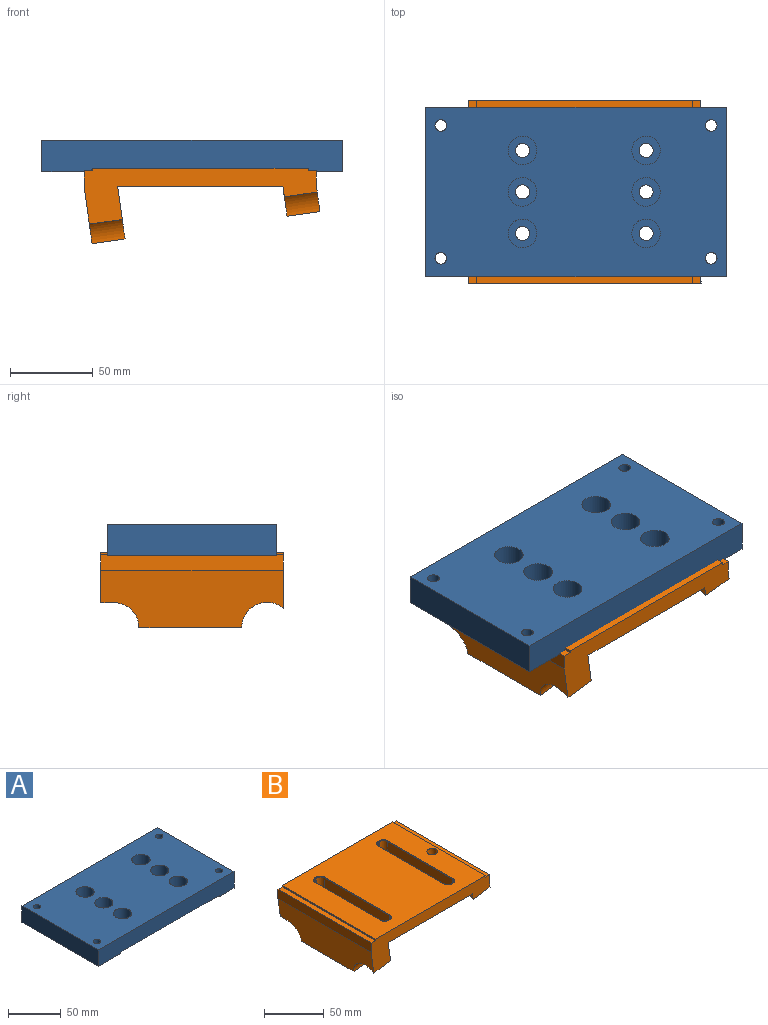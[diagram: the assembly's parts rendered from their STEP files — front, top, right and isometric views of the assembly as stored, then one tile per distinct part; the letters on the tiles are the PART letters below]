
ASSEMBLY  parts=2 mates=1
PART A: 40 faces, bbox 181x102x19 mm
  f0: plane 102x20mm, normal (0,0,-1), area 1721mm2, adj f1,f8,f9,f33,f36,f37
  f1: plane 181x19mm, normal (0,-1,0), area 3242.5mm2, adj f0,f8,f10,f11,f12,f37,f38,f39
  f2: cylinder r=4.25mm len=8.5mm, axis (0,0,1), area 146.9mm2, adj f13,f39
  f3: cylinder r=4.25mm len=8.5mm, axis (0,0,1), area 146.9mm2, adj f15,f39
  f4: cylinder r=4.25mm len=8.5mm, axis (0,0,1), area 146.9mm2, adj f17,f39
  f5: cylinder r=4.25mm len=8.5mm, axis (0,0,1), area 146.9mm2, adj f19,f39
  f6: cylinder r=4.25mm len=8.5mm, axis (0,0,1), area 146.9mm2, adj f21,f39
  f7: cylinder r=4.25mm len=8.5mm, axis (0,0,1), area 146.9mm2, adj f23,f39
  f8: plane 102x19mm, normal (1,0,0), area 1938mm2, adj f0,f1,f9,f11
  f9: plane 181x19mm, normal (0,1,0), area 3242.5mm2, adj f0,f8,f10,f11,f12,f37,f38,f39
  f10: plane 102x19mm, normal (-1,0,0), area 1938mm2, adj f1,f9,f11,f12
  f11: plane 181x102mm, normal (0,0,1), area 16905.8mm2, adj f1,f8,f9,f10,f14,f16,f18,f20
  f12: plane 102x30mm, normal (0,0,-1), area 2741mm2, adj f1,f9,f10,f27,f30,f38
  f13: plane 17.25x17.25mm, normal (0,0,1), area 177mm2, adj f2,f14
  f14: cylinder r=8.62mm len=17.25mm, axis (0,0,1), area 650.3mm2, adj f11,f13
  f15: plane 17.25x17.25mm, normal (0,0,1), area 177mm2, adj f3,f16
  f16: cylinder r=8.62mm len=17.25mm, axis (0,0,1), area 650.3mm2, adj f11,f15
  f17: plane 17.25x17.25mm, normal (0,0,1), area 177mm2, adj f4,f18
  f18: cylinder r=8.62mm len=17.25mm, axis (0,0,1), area 650.3mm2, adj f11,f17
  f19: plane 17.25x17.25mm, normal (0,0,1), area 177mm2, adj f5,f20
  f20: cylinder r=8.62mm len=17.25mm, axis (0,0,1), area 650.3mm2, adj f11,f19
  f21: plane 17.25x17.25mm, normal (0,0,1), area 177mm2, adj f6,f22
  f22: cylinder r=8.62mm len=17.25mm, axis (0,0,1), area 650.3mm2, adj f11,f21
  f23: plane 17.25x17.25mm, normal (0,0,1), area 177mm2, adj f7,f24
  f24: cylinder r=8.62mm len=17.25mm, axis (0,0,1), area 650.3mm2, adj f11,f23
  f25: cylinder r=3.5mm len=11mm, axis (0,0,-1), area 241.9mm2, adj f11,f26
  f26: plane 14.25x14.25mm, normal (0,0,-1), area 121mm2, adj f25,f27
  f27: cylinder r=7.12mm len=14.25mm, axis (0,0,-1), area 358.1mm2, adj f12,f26
  f28: cylinder r=3.5mm len=11mm, axis (0,0,-1), area 241.9mm2, adj f11,f29
  f29: plane 14.25x14.25mm, normal (0,0,-1), area 121mm2, adj f28,f30
  f30: cylinder r=7.12mm len=14.25mm, axis (0,0,-1), area 358.1mm2, adj f12,f29
  f31: cylinder r=3.5mm len=11mm, axis (0,0,-1), area 241.9mm2, adj f11,f32
  f32: plane 14.25x14.25mm, normal (0,0,-1), area 121mm2, adj f31,f33
  f33: cylinder r=7.12mm len=14.25mm, axis (0,0,-1), area 358.1mm2, adj f0,f32
  f34: cylinder r=3.5mm len=11mm, axis (0,0,-1), area 241.9mm2, adj f11,f35
  f35: plane 14.25x14.25mm, normal (0,0,-1), area 121mm2, adj f34,f36
  f36: cylinder r=7.12mm len=14.25mm, axis (0,0,-1), area 358.1mm2, adj f0,f35
  f37: plane 102x1.5mm, normal (-1,0,0), area 153mm2, adj f0,f1,f9,f39
  f38: plane 102x1.5mm, normal (1,0,0), area 153mm2, adj f1,f9,f12,f39
  f39: plane 131x102mm, normal (0,0,-1), area 13021.5mm2, adj f1,f2,f3,f4,f5,f6,f7,f9
PART B: 74 faces, bbox 142.4x110.3x47 mm
  f0: plane 130.27x110.27mm, normal (0,0,1), area 12364.7mm2, adj f1,f12,f53,f54,f55,f56,f57,f58
  f1: plane 140.48x33.73mm, normal (0,-1,0), area 2053.4mm2, adj f0,f2,f4,f5,f6,f7,f9,f10
  f2: plane 110x99.61mm, normal (0,0,-1), area 9085.7mm2, adj f1,f9,f10,f12,f37,f38,f39,f40
  f3: plane 98.95x15.18mm, normal (0.99,0,0.14), area 1051.1mm2, adj f6,f11,f12,f14,f15,f16
  f4: plane 110x34.47mm, normal (-0.99,0,-0.14), area 3204.6mm2, adj f1,f7,f8,f12,f13,f17,f18
  f5: plane 8.46x3.44mm, normal (0.99,0,0.14), area 10.4mm2, adj f1,f6,f14
  f6: plane 110.02x9.52mm, normal (1,0,0), area 1044.9mm2, adj f1,f3,f5,f12,f14,f71
  f7: plane 110x9.5mm, normal (-1,0,0), area 1045mm2, adj f1,f4,f12,f73
  f8: plane 62x19.81mm, normal (0.14,0,-0.99), area 1176.4mm2, adj f4,f9,f13,f17,f28
  f9: plane 110x31.69mm, normal (0.99,0,0.14), area 2895.4mm2, adj f1,f2,f8,f12,f13,f17,f18
  f10: plane 110x17.96mm, normal (-0.99,0,-0.14), area 1370.5mm2, adj f1,f2,f11,f12,f14,f15,f16
  f11: plane 62x19.81mm, normal (0.14,0,-0.99), area 1176.4mm2, adj f3,f10,f14,f15,f69
  f12: plane 140.01x30.38mm, normal (0,1,0), area 1918.2mm2, adj f0,f2,f3,f4,f6,f7,f9,f10
  f13: cylinder r=15.25mm len=25mm, axis (-0.99,0,-0.14), area 693.3mm2, adj f1,f4,f8,f9
  f14: cylinder r=15.25mm len=25mm, axis (-0.99,0,-0.14), area 693.3mm2, adj f1,f3,f5,f6,f10,f11
  f15: cylinder r=15.25mm len=21.93mm, axis (-0.99,0,-0.14), area 479.1mm2, adj f3,f10,f11,f16
  f16: plane 19.81x7.75mm, normal (0.14,0,-0.99), area 155mm2, adj f3,f10,f12,f15
  f17: cylinder r=15.25mm len=21.93mm, axis (-0.99,0,-0.14), area 479.1mm2, adj f4,f8,f9,f18
  f18: plane 19.81x7.75mm, normal (0.14,0,-0.99), area 155mm2, adj f4,f9,f12,f17
  f19: plane 10x1mm, normal (0,1,0), area 10mm2, adj f29,f32,f48,f56
  f20: plane 77x10mm, normal (-1,0,0), area 770mm2, adj f29,f30,f45,f53
  f21: plane 10x1mm, normal (0,-1,0), area 10mm2, adj f30,f31,f49,f57
  f22: plane 77x10mm, normal (1,0,0), area 770mm2, adj f31,f32,f52,f60
  f23: plane 10x1mm, normal (0,1,0), area 10mm2, adj f33,f36,f39,f67
  f24: plane 77x10mm, normal (-1,0,0), area 770mm2, adj f35,f36,f38,f66
  f25: plane 10x1mm, normal (0,-1,0), area 10mm2, adj f34,f35,f42,f62
  f26: plane 77x10mm, normal (1,0,0), area 770mm2, adj f33,f34,f43,f63
  f27: cone r=0mm half-angle=59deg, axis (0.14,0,-0.99), area 74.2mm2, adj f28
  f28: cylinder r=4.5mm len=33.93mm, axis (0.14,0,-0.99), area 933.1mm2, adj f8,f27
  f29: cylinder r=4.5mm len=10mm, axis (0,0,1), area 70.7mm2, adj f19,f20,f46,f54
  f30: cylinder r=4.5mm len=10mm, axis (0,0,-1), area 70.7mm2, adj f20,f21,f47,f55
  f31: cylinder r=4.5mm len=10mm, axis (0,0,1), area 70.7mm2, adj f21,f22,f51,f59
  f32: cylinder r=4.5mm len=10mm, axis (0,0,-1), area 70.7mm2, adj f19,f22,f50,f58
  f33: cylinder r=4.5mm len=10mm, axis (0,0,-1), area 70.7mm2, adj f23,f26,f41,f65
  f34: cylinder r=4.5mm len=10mm, axis (0,0,1), area 70.7mm2, adj f25,f26,f44,f61
  f35: cylinder r=4.5mm len=10mm, axis (0,0,-1), area 70.7mm2, adj f24,f25,f40,f64
  f36: cylinder r=4.5mm len=10mm, axis (0,0,1), area 70.7mm2, adj f23,f24,f37,f68
  f37: torus R=5mm, axis (0,0,1), area 5.8mm2, adj f2,f36,f38,f39
  f38: cylinder r=0.5mm len=77mm, axis (0,1,0), area 60.5mm2, adj f2,f24,f37,f40
  f39: cylinder r=0.5mm len=1mm, axis (1,0,0), area 0.8mm2, adj f2,f23,f37,f41
  f40: torus R=5mm, axis (0,0,1), area 5.8mm2, adj f2,f35,f38,f42
  f41: torus R=5mm, axis (0,0,1), area 5.8mm2, adj f2,f33,f39,f43
  f42: cylinder r=0.5mm len=1mm, axis (-1,0,0), area 0.8mm2, adj f2,f25,f40,f44
  f43: cylinder r=0.5mm len=77mm, axis (0,-1,0), area 60.5mm2, adj f2,f26,f41,f44
  f44: torus R=5mm, axis (0,0,1), area 5.8mm2, adj f2,f34,f42,f43
  f45: cylinder r=0.5mm len=77mm, axis (0,1,0), area 60.5mm2, adj f2,f20,f46,f47
  f46: torus R=5mm, axis (0,0,1), area 5.8mm2, adj f2,f29,f45,f48
  f47: torus R=5mm, axis (0,0,1), area 5.8mm2, adj f2,f30,f45,f49
  f48: cylinder r=0.5mm len=1mm, axis (1,0,0), area 0.8mm2, adj f2,f19,f46,f50
  f49: cylinder r=0.5mm len=1mm, axis (-1,0,0), area 0.8mm2, adj f2,f21,f47,f51
  f50: torus R=5mm, axis (0,0,1), area 5.8mm2, adj f2,f32,f48,f52
  f51: torus R=5mm, axis (0,0,1), area 5.8mm2, adj f2,f31,f49,f52
  f52: cylinder r=0.5mm len=77mm, axis (0,-1,0), area 60.5mm2, adj f2,f22,f50,f51
  f53: cylinder r=0.5mm len=77mm, axis (0,-1,0), area 60.5mm2, adj f0,f20,f54,f55
  f54: torus R=5mm, axis (0,0,1), area 5.8mm2, adj f0,f29,f53,f56
  f55: torus R=5mm, axis (0,0,1), area 5.8mm2, adj f0,f30,f53,f57
  f56: cylinder r=0.5mm len=1mm, axis (-1,0,0), area 0.8mm2, adj f0,f19,f54,f58
  f57: cylinder r=0.5mm len=1mm, axis (1,0,0), area 0.8mm2, adj f0,f21,f55,f59
  f58: torus R=5mm, axis (0,0,1), area 5.8mm2, adj f0,f32,f56,f60
  f59: torus R=5mm, axis (0,0,1), area 5.8mm2, adj f0,f31,f57,f60
  f60: cylinder r=0.5mm len=77mm, axis (0,1,0), area 60.5mm2, adj f0,f22,f58,f59
  f61: torus R=5mm, axis (0,0,1), area 5.8mm2, adj f0,f34,f62,f63
  f62: cylinder r=0.5mm len=1mm, axis (1,0,0), area 0.8mm2, adj f0,f25,f61,f64
  f63: cylinder r=0.5mm len=77mm, axis (0,1,0), area 60.5mm2, adj f0,f26,f61,f65
  f64: torus R=5mm, axis (0,0,1), area 5.8mm2, adj f0,f35,f62,f66
  f65: torus R=5mm, axis (0,0,1), area 5.8mm2, adj f0,f33,f63,f67
  f66: cylinder r=0.5mm len=77mm, axis (0,-1,0), area 60.5mm2, adj f0,f24,f64,f68
  f67: cylinder r=0.5mm len=1mm, axis (-1,0,0), area 0.8mm2, adj f0,f23,f65,f68
  f68: torus R=5mm, axis (0,0,1), area 5.8mm2, adj f0,f36,f66,f67
  f69: cylinder r=4.5mm len=29.45mm, axis (0.14,0,-0.99), area 787.2mm2, adj f0,f11
  f70: plane 110x1.5mm, normal (1,0,0), area 165mm2, adj f0,f1,f12,f71
  f71: plane 110x5mm, normal (0,0,1), area 550mm2, adj f1,f6,f12,f70
  f72: plane 110x1.5mm, normal (-1,0,0), area 165mm2, adj f0,f1,f12,f73
  f73: plane 110x5mm, normal (0,0,1), area 550mm2, adj f1,f7,f12,f72
PLACE A t=(-19.13,-76.16,11.5)mm
PLACE B t=(-20.58,-21.16,-20.34)mm fixed
MATE slider B.f72 <-> A.f38  axis (-1,0,0) through (-79.15,-76.16,12.25)mm
